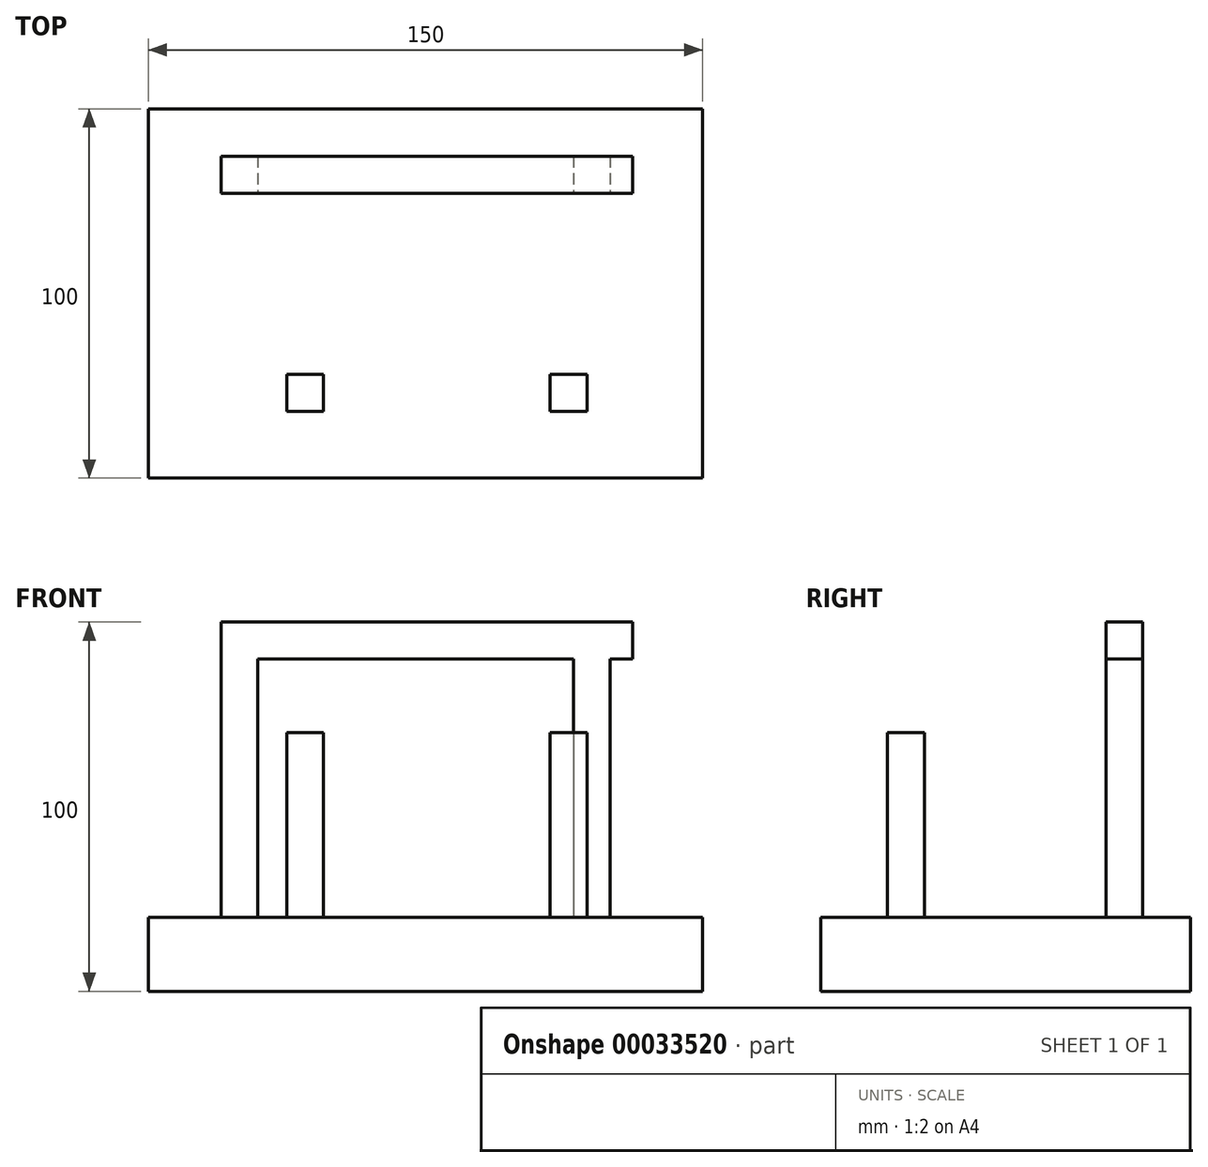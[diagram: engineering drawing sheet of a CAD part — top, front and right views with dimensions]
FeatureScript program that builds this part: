
annotation { "Feature Type Name" : "Feature", "Feature Type Description" : "" }
export const myFeature = defineFeature(function(context is Context, id is Id, definition is map)
    precondition{}
    {
        {
            var Q0;
            Q0=qCreatedBy(makeId("Top.planeOp"),FACE);
            var sketch = newSketch(context, id + "F0", { "sketchPlane" : qUnion([Q0])});
            skLineSegment(sketch, "E0.bottom", {"start": v(-19.62, 99.5) * mm, "end": v(130.38, 99.5) * mm});
            skLineSegment(sketch, "E0.top", {"start": v(-19.62, -0.5) * mm, "end": v(130.38, -0.5) * mm});
            skLineSegment(sketch, "E0.left", {"start": v(-19.62, 99.5) * mm, "end": v(-19.62, -0.5) * mm});
            skLineSegment(sketch, "E0.right", {"start": v(130.38, 99.5) * mm, "end": v(130.38, -0.5) * mm});
            skSolve(sketch);
        }
        {
            var Q0;
            Q0=makeQuery(id+"F0.imprint","IMPRINT",FACE,{"disambiguationData":[TD([[makeQuery(id+"F0.imprint","IMPRINT",EDGE,{"derivedFrom":sQuery(id+"F0.wireOp",EDGE,"E0.bottom")}),-1.0]])]});
            extrude(context, id + "F1", {"entities" : qUnion([Q0]), "depth" : 20 * mm});
        }
        {
            var Q0;
            Q0=makeQuery(id+"F1.opExtrude","CAP_FACE",FACE,{"disambiguationData":[OSD([sQuery(id+"F0.wireOp",EDGE,"E0.bottom"),sQuery(id+"F0.wireOp",EDGE,"E0.top"),sQuery(id+"F0.wireOp",EDGE,"E0.left"),sQuery(id+"F0.wireOp",EDGE,"E0.right")])],"isStart":false});
            var sketch = newSketch(context, id + "F2", { "sketchPlane" : qUnion([Q0])});
            skLineSegment(sketch, "E1.bottom", {"start": v(0, 86.63) * mm, "end": v(10, 86.63) * mm});
            skLineSegment(sketch, "E1.top", {"start": v(0, 76.63) * mm, "end": v(10, 76.63) * mm});
            skLineSegment(sketch, "E1.left", {"start": v(0, 86.63) * mm, "end": v(0, 76.63) * mm});
            skLineSegment(sketch, "E1.right", {"start": v(10, 86.63) * mm, "end": v(10, 76.63) * mm});
            skLineSegment(sketch, "E2.bottom", {"start": v(95.38, 86.63) * mm, "end": v(105.38, 86.63) * mm});
            skLineSegment(sketch, "E2.top", {"start": v(95.38, 76.63) * mm, "end": v(105.38, 76.63) * mm});
            skLineSegment(sketch, "E2.left", {"start": v(95.38, 86.63) * mm, "end": v(95.38, 76.63) * mm});
            skLineSegment(sketch, "E2.right", {"start": v(105.38, 86.63) * mm, "end": v(105.38, 76.63) * mm});
            skLineSegment(sketch, "E3.bottom", {"start": v(17.78, 27.55) * mm, "end": v(27.79, 27.55) * mm});
            skLineSegment(sketch, "E3.top", {"start": v(17.78, 17.55) * mm, "end": v(27.79, 17.55) * mm});
            skLineSegment(sketch, "E3.left", {"start": v(17.78, 27.55) * mm, "end": v(17.78, 17.55) * mm});
            skLineSegment(sketch, "E3.right", {"start": v(27.79, 27.55) * mm, "end": v(27.79, 17.55) * mm});
            skLineSegment(sketch, "E4.bottom", {"start": v(99.1, 27.56) * mm, "end": v(89.1, 27.56) * mm});
            skLineSegment(sketch, "E4.top", {"start": v(99.1, 17.56) * mm, "end": v(89.1, 17.56) * mm});
            skLineSegment(sketch, "E4.left", {"start": v(99.1, 27.56) * mm, "end": v(99.1, 17.56) * mm});
            skLineSegment(sketch, "E4.right", {"start": v(89.1, 27.56) * mm, "end": v(89.1, 17.56) * mm});
            skSolve(sketch);
        }
        {
            var Q0;
            Q0=makeQuery(id+"F2.imprint","IMPRINT",FACE,{"disambiguationData":[TD([[makeQuery(id+"F2.imprint","IMPRINT",EDGE,{"derivedFrom":sQuery(id+"F2.wireOp",EDGE,"E1.bottom")}),-1.0]])]});
            var Q1;
            Q1=makeQuery(id+"F2.imprint","IMPRINT",FACE,{"disambiguationData":[TD([[makeQuery(id+"F2.imprint","IMPRINT",EDGE,{"derivedFrom":sQuery(id+"F2.wireOp",EDGE,"E2.bottom")}),-1.0]])]});
            extrude(context, id + "F3", {"entities" : qUnion([Q0, Q1]), "operationType" : NewBodyOperationType.ADD, "depth" : 70 * mm});
        }
        {
            var Q0;
            Q0=makeQuery(id+"F2.imprint","IMPRINT",FACE,{"disambiguationData":[TD([[makeQuery(id+"F2.imprint","IMPRINT",EDGE,{"derivedFrom":sQuery(id+"F2.wireOp",EDGE,"E3.bottom")}),-1.0]])]});
            var Q1;
            Q1=makeQuery(id+"F2.imprint","IMPRINT",FACE,{"disambiguationData":[TD([[makeQuery(id+"F2.imprint","IMPRINT",EDGE,{"derivedFrom":sQuery(id+"F2.wireOp",EDGE,"E4.bottom")}),1.0]])]});
            extrude(context, id + "F4", {"entities" : qUnion([Q0, Q1]), "operationType" : NewBodyOperationType.ADD, "depth" : 50 * mm});
        }
        {
            var Q0;
            Q0=makeQuery(id+"F3.opExtrude","CAP_FACE",FACE,{"disambiguationData":[OSD([sQuery(id+"F2.wireOp",EDGE,"E1.bottom"),sQuery(id+"F2.wireOp",EDGE,"E1.top"),sQuery(id+"F2.wireOp",EDGE,"E1.left"),sQuery(id+"F2.wireOp",EDGE,"E1.right")])],"isStart":false});
            var sketch = newSketch(context, id + "F5", { "sketchPlane" : qUnion([Q0])});
            skLineSegment(sketch, "E5.bottom", {"start": v(0, 86.63) * mm, "end": v(111.45, 86.63) * mm});
            skLineSegment(sketch, "E5.top", {"start": v(0, 76.63) * mm, "end": v(111.45, 76.63) * mm});
            skLineSegment(sketch, "E5.left", {"start": v(0, 86.63) * mm, "end": v(0, 76.63) * mm});
            skLineSegment(sketch, "E5.right", {"start": v(111.45, 86.63) * mm, "end": v(111.45, 76.63) * mm});
            skSolve(sketch);
        }
        {
            var Q0;
            Q0 = qSketchRegion(id + "F5", true);
            extrude(context, id + "F6", {"entities" : qUnion([Q0]), "operationType" : NewBodyOperationType.ADD, "depth" : 10 * mm});
        }
    });
